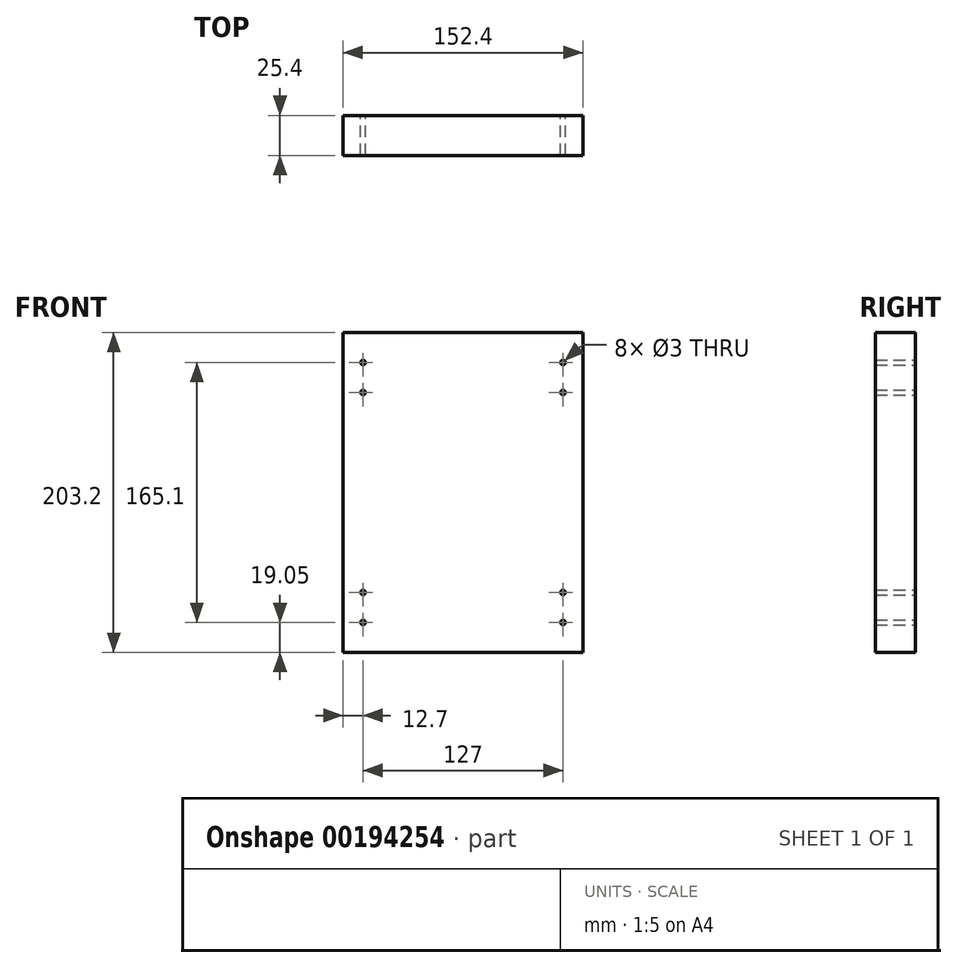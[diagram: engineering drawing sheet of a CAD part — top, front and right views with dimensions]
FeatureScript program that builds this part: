
annotation { "Feature Type Name" : "Feature", "Feature Type Description" : "" }
export const myFeature = defineFeature(function(context is Context, id is Id, definition is map)
    precondition{}
    {
        {
            var Q0;
            Q0=qCreatedBy(makeId("Front.planeOp"),FACE);
            var sketch = newSketch(context, id + "F0", { "sketchPlane" : qUnion([Q0])});
            skLineSegment(sketch, "E0.bottom", {"start": v(-76.2, 101.6) * mm, "end": v(76.2, 101.6) * mm});
            skLineSegment(sketch, "E0.top", {"start": v(-76.2, -101.6) * mm, "end": v(76.2, -101.6) * mm});
            skLineSegment(sketch, "E0.left", {"start": v(-76.2, 101.6) * mm, "end": v(-76.2, -101.6) * mm});
            skLineSegment(sketch, "E0.right", {"start": v(76.2, 101.6) * mm, "end": v(76.2, -101.6) * mm});
            skPoint(sketch, "E0.middle", {"position": v(0, 0) * mm});
            skLineSegment(sketch, "E1", {"start": v(-63.5, 101.6) * mm, "end": v(-63.5, 82.55) * mm});
            skLineSegment(sketch, "E2", {"start": v(-63.5, 82.55) * mm, "end": v(-63.5, 63.5) * mm});
            skLineSegment(sketch, "E3", {"start": v(-76.2, 101.6) * mm, "end": v(-63.5, 101.6) * mm});
            skLineSegment(sketch, "E4", {"start": v(-63.5, 101.6) * mm, "end": v(-76.2, 101.6) * mm});
            skCircle(sketch, "E5", {"center": v(-63.5, 82.55) * mm, "radius": 1.5 * mm});
            skCircle(sketch, "E6", {"center": v(-63.5, 63.5) * mm, "radius": 1.5 * mm});
            skLineSegment(sketch, "E7", {"start": v(63.5, 101.6) * mm, "end": v(63.5, 82.55) * mm});
            skLineSegment(sketch, "E8", {"start": v(63.5, 82.55) * mm, "end": v(63.5, 63.5) * mm});
            skLineSegment(sketch, "E9", {"start": v(63.5, 101.6) * mm, "end": v(76.2, 101.6) * mm});
            skCircle(sketch, "E10", {"center": v(63.5, 82.55) * mm, "radius": 1.5 * mm});
            skCircle(sketch, "E11", {"center": v(63.5, 63.5) * mm, "radius": 1.5 * mm});
            skLineSegment(sketch, "E12", {"start": v(-63.5, -101.6) * mm, "end": v(-63.5, -82.55) * mm});
            skLineSegment(sketch, "E13", {"start": v(-63.5, -82.55) * mm, "end": v(-63.5, -63.5) * mm});
            skLineSegment(sketch, "E14", {"start": v(-76.2, -101.6) * mm, "end": v(-63.5, -101.6) * mm});
            skLineSegment(sketch, "E15", {"start": v(63.5, -101.6) * mm, "end": v(63.5, -82.55) * mm});
            skLineSegment(sketch, "E16", {"start": v(63.5, -82.55) * mm, "end": v(63.5, -63.5) * mm});
            skLineSegment(sketch, "E17", {"start": v(63.5, -101.6) * mm, "end": v(76.2, -101.6) * mm});
            skLineSegment(sketch, "E18", {"start": v(76.2, -101.6) * mm, "end": v(63.5, -101.6) * mm});
            skCircle(sketch, "E19", {"center": v(-63.5, -63.5) * mm, "radius": 1.5 * mm});
            skCircle(sketch, "E20", {"center": v(-63.5, -82.55) * mm, "radius": 1.5 * mm});
            skCircle(sketch, "E21", {"center": v(63.5, -63.5) * mm, "radius": 1.5 * mm});
            skCircle(sketch, "E22", {"center": v(63.5, -82.55) * mm, "radius": 1.5 * mm});
            skSolve(sketch);
        }
        {
            var Q0;
            Q0=makeQuery(id+"F0.imprint","IMPRINT",FACE,{"disambiguationData":[TD([[makeQuery(id+"F0.imprint","IMPRINT",EDGE,{"derivedFrom":sQuery(id+"F0.wireOp",EDGE,"E0.bottom")}),-1.0]])]});
            extrude(context, id + "F1", {"entities" : qUnion([Q0]), "depth" : 25.4 * mm});
        }
    });
